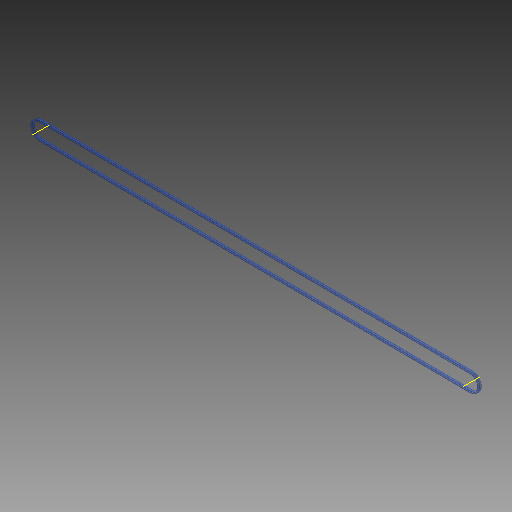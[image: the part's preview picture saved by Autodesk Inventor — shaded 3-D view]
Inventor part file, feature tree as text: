
AUTODESK INVENTOR PART (.ipt)
format: ipt  version: 2017 (Build 210142000, 142)  size: 137,216 bytes
history: native  units: mm
features: other x5, plane x2, pattern_linear x1
ambient origin geometry x8: Origin, YZ Plane, XZ Plane, XY Plane, X Axis, Y Axis, Z Axis, Center Point
bodies: Solid1 (feature_tree), Solid (feature_tree)
feature tree (8):
  other  "Work Axis1"
  other  "Work Axis2"
  plane  "Work Plane2"
  plane  "Work Plane3"
  other  "Path"
  other  "Section Plane"
  pattern_linear  "Strand Pattern"  Spacing1=0.0mm  [1 undecoded]
  other  "Section Sketch"
note: 1 required parameter value undecoded (feature->parameter linkage not recoverable at this tier; creation-order binding heuristic only, values carry confidence <= 0.55)
